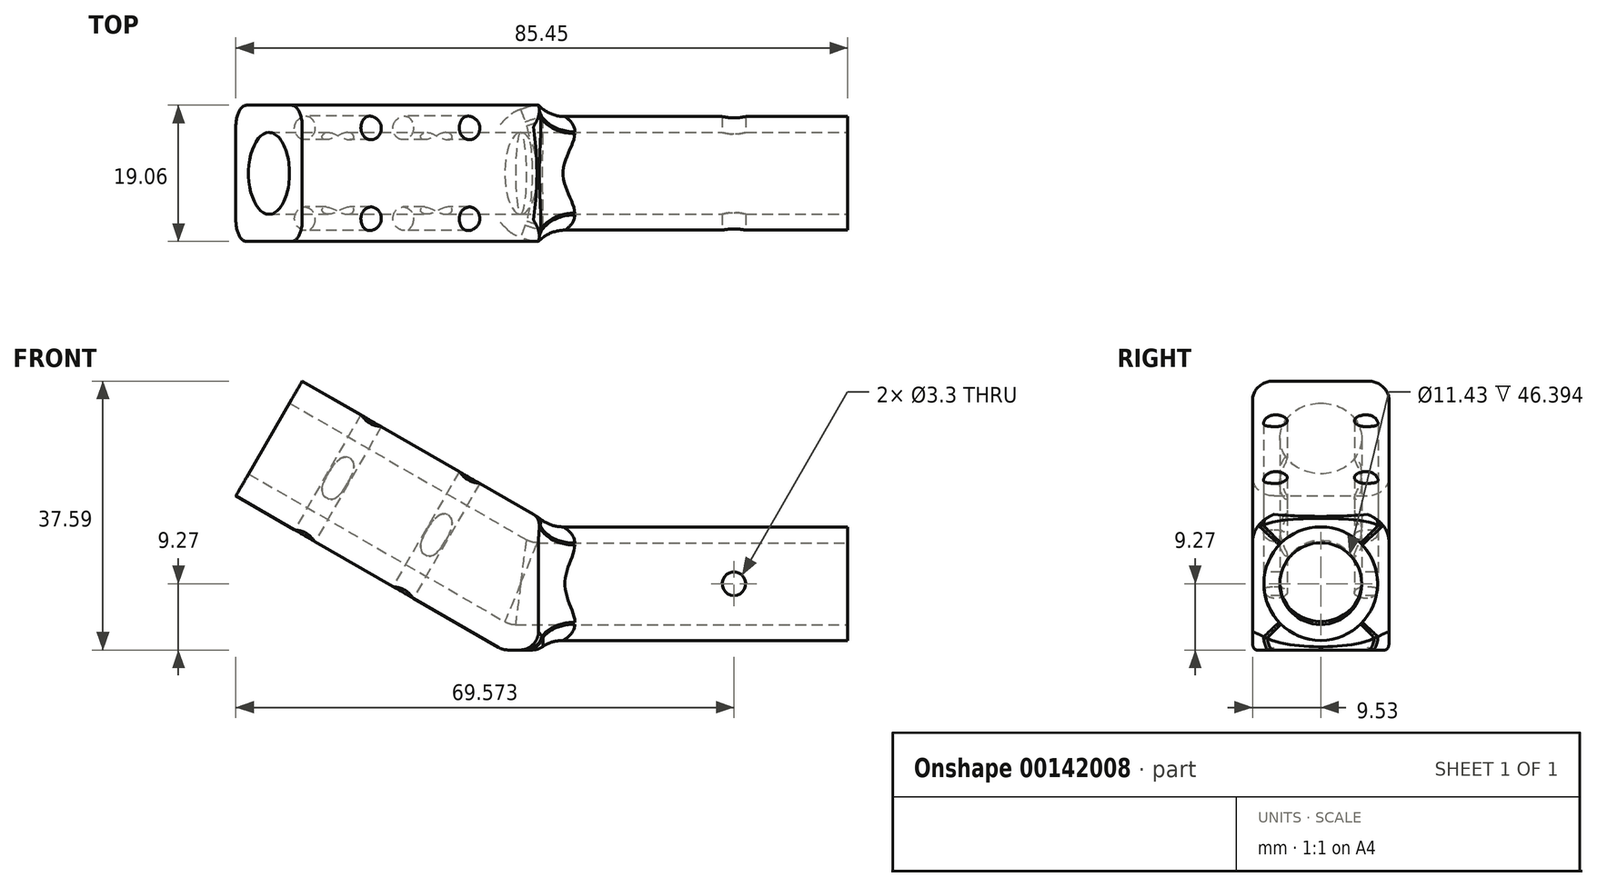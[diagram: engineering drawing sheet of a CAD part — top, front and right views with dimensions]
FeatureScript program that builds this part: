
annotation { "Feature Type Name" : "Feature", "Feature Type Description" : "" }
export const myFeature = defineFeature(function(context is Context, id is Id, definition is map)
    precondition{}
    {
        {
            var Q0;
            Q0=qCreatedBy(makeId("Front.planeOp"),FACE);
            var sketch = newSketch(context, id + "F0", { "sketchPlane" : qUnion([Q0])});
            skLineSegment(sketch, "E0.bottom", {"start": v(4.97, 9.27) * mm, "end": v(48.15, 9.27) * mm});
            skLineSegment(sketch, "E0.top", {"start": v(0, -9.27) * mm, "end": v(48.15, -9.27) * mm});
            skLineSegment(sketch, "E0.right", {"start": v(48.15, 9.27) * mm, "end": v(48.15, -9.27) * mm});
            skLineSegment(sketch, "E1", {"start": v(0, 0) * mm, "end": v(48.15, 0) * mm, "construction": true});
            skLineSegment(sketch, "E2", {"start": v(4.97, 9.27) * mm, "end": v(-28.03, 28.32) * mm});
            skLineSegment(sketch, "E3", {"start": v(-37.3, 12.26) * mm, "end": v(-28.03, 28.32) * mm});
            skPoint(sketch, "E4.orphan", {"position": v(0, 13.5) * mm});
            skLineSegment(sketch, "E5", {"start": v(-37.3, 12.26) * mm, "end": v(0, -9.27) * mm});
            skSolve(sketch);
        }
        {
            var Q0;
            Q0 = qSketchRegion(id + "F0", true);
            extrude(context, id + "F1", {"entities" : qUnion([Q0]), "depth" : 9.52 * mm, "hasSecondDirection" : true, "secondDirectionOppositeDirection" : true, "secondDirectionDepth" : 9.52 * mm});
        }
        {
            var Q0;
            Q0=makeQuery(id+"F1.opExtrude","SWEPT_FACE",FACE,{"disambiguationData":[OSD([sQuery(id+"F0.wireOp",EDGE,"E5")])]});
            var sketch = newSketch(context, id + "F2", { "sketchPlane" : qUnion([Q0])});
            skLineSegment(sketch, "E6.bottom", {"start": v(-38.43, -9.53) * mm, "end": v(-0.33, -9.53) * mm});
            skLineSegment(sketch, "E6.top", {"start": v(-38.43, 9.53) * mm, "end": v(-0.33, 9.53) * mm});
            skLineSegment(sketch, "E6.left", {"start": v(-38.43, -9.53) * mm, "end": v(-38.43, 9.53) * mm});
            skLineSegment(sketch, "E6.right", {"start": v(-0.33, -9.52) * mm, "end": v(-0.33, 9.53) * mm});
            skLineSegment(sketch, "E7", {"start": v(-38.43, 0) * mm, "end": v(-0.33, 0) * mm, "construction": true});
            skLineSegment(sketch, "E8", {"start": v(-19.38, 9.53) * mm, "end": v(-19.38, -9.53) * mm, "construction": true});
            skLineSegment(sketch, "E9.bottom", {"start": v(-27.32, -6.35) * mm, "end": v(-11.45, -6.35) * mm, "construction": true});
            skLineSegment(sketch, "E9.top", {"start": v(-27.32, 6.35) * mm, "end": v(-11.45, 6.35) * mm, "construction": true});
            skLineSegment(sketch, "E9.left", {"start": v(-27.32, -6.35) * mm, "end": v(-27.32, 6.35) * mm, "construction": true});
            skLineSegment(sketch, "E9.right", {"start": v(-11.45, -6.35) * mm, "end": v(-11.45, 6.35) * mm, "construction": true});
            skPoint(sketch, "E9.middle", {"position": v(-19.38, 0) * mm});
            skSolve(sketch);
        }
        {
            var Q0;
            Q0=sQuery(id+"F2.wireOp",VERTEX,"E9.left.end");
            var Q1;
            Q1=sQuery(id+"F2.wireOp",VERTEX,"E9.left.start");
            var Q2;
            Q2=sQuery(id+"F2.wireOp",VERTEX,"E9.right.start");
            var Q3;
            Q3=sQuery(id+"F2.wireOp",VERTEX,"E9.top.end");
            var Q4;
            Q4=makeQuery(id+"F1.opExtrude","SWEPT_BODY",BODY,{"disambiguationData":[OSD([sQuery(id+"F0.wireOp",EDGE,"E0.bottom"),sQuery(id+"F0.wireOp",EDGE,"E0.top"),sQuery(id+"F0.wireOp",EDGE,"E0.right"),sQuery(id+"F0.wireOp",EDGE,"E2"),sQuery(id+"F0.wireOp",EDGE,"95kfVAff-3bN3-xnc1-YnyT-jtpb1TC5GENx"),sQuery(id+"F0.wireOp",EDGE,"E3")])]});
            hole(context, id + "F3", {"style" : HoleStyle.SIMPLE, "endStyle" : HoleEndStyle.THROUGH, "standardTappedOrClearance" : lookupTablePath({ "standard" : "ISO", "fit" : "Normal", "size" : "M3", "type" : "Clearance" }), "standardBlindInLast" : lookupTablePath({ "fit" : "Standard", "standard" : "ISO", "size" : "M3", "type" : "Clearance" }), "holeDiameter" : 3.3 * mm, "locations" : qUnion([Q0, Q1, Q2, Q3]), "scope" : qUnion([Q4]), "isTappedThrough" : true});
        }
        {
            var Q0;
            Q0=makeQuery(id+"F1.opExtrude","SWEPT_FACE",FACE,{"disambiguationData":[OSD([sQuery(id+"F0.wireOp",EDGE,"E3")])]});
            var sketch = newSketch(context, id + "F4", { "sketchPlane" : qUnion([Q0])});
            skLineSegment(sketch, "E10", {"start": v(0, 10.51) * mm, "end": v(0, -8.03) * mm, "construction": true});
            skCircle(sketch, "E11", {"center": v(0, 1.24) * mm, "radius": 5.72 * mm});
            skSolve(sketch);
        }
        {
            var Q0;
            Q0=qCreatedBy(makeId("Front.planeOp"),FACE);
            var sketch = newSketch(context, id + "F5", { "sketchPlane" : qUnion([Q0])});
            skLineSegment(sketch, "E12", {"start": v(-32.66, 20.3) * mm, "end": v(2.48, 0) * mm});
            skLineSegment(sketch, "E13", {"start": v(2.48, 0) * mm, "end": v(48.15, 0) * mm});
            skPoint(sketch, "E14", {"position": v(48.15, 0) * mm});
            skSolve(sketch);
        }
        {
            var Q0;
            Q0 = qSketchRegion(id + "F4", true);
            var Q1;
            Q1 = qConstructionFilter(qBodyType(qCreatedBy(id + "F5" ,EDGE), BodyType.WIRE), ConstructionObject.NO);
            sweep(context, id + "F6", {"operationType" : NewBodyOperationType.REMOVE, "profiles" : qUnion([Q0]), "path" : qUnion([Q1])});
        }
        {
            var Q0;
            Q0=makeQuery(id+"F1.opExtrude","SWEPT_FACE",FACE,{"disambiguationData":[OSD([sQuery(id+"F0.wireOp",EDGE,"E0.right")])]});
            var sketch = newSketch(context, id + "F7", { "sketchPlane" : qUnion([Q0])});
            skCircle(sketch, "E15", {"center": v(0, 0) * mm, "radius": 7.94 * mm});
            skLineSegment(sketch, "E16.0.0", {"start": v(9.53, -9.27) * mm, "end": v(9.53, 9.27) * mm});
            skLineSegment(sketch, "E16.0.1", {"start": v(9.52, 9.27) * mm, "end": v(-9.53, 9.27) * mm});
            skLineSegment(sketch, "E16.0.2", {"start": v(-9.53, 9.27) * mm, "end": v(-9.53, -9.27) * mm});
            skLineSegment(sketch, "E16.0.3", {"start": v(-9.53, -9.27) * mm, "end": v(9.52, -9.27) * mm});
            skSolve(sketch);
        }
        {
            var Q0;
            Q0 = qSketchRegion(id + "F7", true);
            extrude(context, id + "F8", {"entities" : qUnion([Q0]), "operationType" : NewBodyOperationType.REMOVE, "oppositeDirection" : true, "depth" : 43.18 * mm});
        }
        {
            var Q0;
            Q0=makeQuery(id+"F8.boolean.opBoolean","COPY",EDGE,{"derivedFrom":makeQuery(id+"F8.opExtrude","CAP_EDGE",EDGE,{"disambiguationData":[OSD([sQuery(id+"F7.wireOp",EDGE,"E15")])],"isStart":false})});
            fillet(context, id + "F9", {"entities" : qUnion([Q0]), "radius" : 5.08 * mm, "tangentPropagation" : true, "allowEdgeOverflow" : false});
        }
        {
            var Q0;
            Q0=makeQuery(id+"F9.opFillet","BLEND_EDGE",EDGE,{"blendedFrom":[makeQuery(id+"F8.boolean.opBoolean","COPY",EDGE,{"derivedFrom":makeQuery(id+"F8.opExtrude","CAP_EDGE",EDGE,{"disambiguationData":[OSD([sQuery(id+"F7.wireOp",EDGE,"E15")])],"isStart":false})}),makeQuery(id+"F1.opExtrude","SWEPT_FACE",FACE,{"disambiguationData":[OSD([sQuery(id+"F0.wireOp",EDGE,"E2")])]})],"blendedInto":[makeQuery(id+"F1.opExtrude","SWEPT_FACE",FACE,{"disambiguationData":[OSD([sQuery(id+"F0.wireOp",EDGE,"E2")])]})]});
            var Q1;
            Q1=makeQuery(id+"F9.opFillet","BLEND_EDGE",EDGE,{"blendedFrom":[makeQuery(id+"F8.boolean.opBoolean","COPY",EDGE,{"derivedFrom":makeQuery(id+"F8.opExtrude","CAP_EDGE",EDGE,{"disambiguationData":[OSD([sQuery(id+"F7.wireOp",EDGE,"E15")])],"isStart":false})}),makeQuery(id+"F1.opExtrude","SWEPT_FACE",FACE,{"disambiguationData":[OSD([sQuery(id+"F0.wireOp",EDGE,"E0.top")])]})],"blendedInto":[makeQuery(id+"F1.opExtrude","SWEPT_FACE",FACE,{"disambiguationData":[OSD([sQuery(id+"F0.wireOp",EDGE,"E0.top")])]})]});
            fillet(context, id + "F10", {"entities" : qUnion([Q0, Q1]), "radius" : 2.54 * mm, "tangentPropagation" : true, "allowEdgeOverflow" : false});
        }
        {
            var Q0;
            Q0=makeQuery(id+"F1.opExtrude","SWEPT_FACE",FACE,{"disambiguationData":[OSD([sQuery(id+"F0.wireOp",EDGE,"E2")])]});
            var sketch = newSketch(context, id + "F11", { "sketchPlane" : qUnion([Q0])});
            skCircle(sketch, "E17.0", {"center": v(-27.32, -6.35) * mm, "radius": 1.65 * mm});
            skCircle(sketch, "E17.1", {"center": v(-27.32, 6.35) * mm, "radius": 1.65 * mm});
            skCircle(sketch, "E17.2", {"center": v(-11.45, -6.35) * mm, "radius": 1.65 * mm});
            skCircle(sketch, "E17.3", {"center": v(-11.45, 6.35) * mm, "radius": 1.65 * mm});
            skCircle(sketch, "E18", {"center": v(-27.32, -6.35) * mm, "radius": 3.18 * mm});
            skCircle(sketch, "E19", {"center": v(-27.32, 6.35) * mm, "radius": 3.18 * mm});
            skCircle(sketch, "E20", {"center": v(-11.45, 6.35) * mm, "radius": 3.18 * mm});
            skCircle(sketch, "E21", {"center": v(-11.45, -6.35) * mm, "radius": 3.18 * mm});
            skSolve(sketch);
        }
        {
            var Q0;
            Q0=makeQuery(id+"F1.opExtrude","CAP_EDGE",EDGE,{"disambiguationData":[OSD([sQuery(id+"F0.wireOp",EDGE,"E2")])],"isStart":true});
            var Q1;
            Q1=makeQuery(id+"F1.opExtrude","CAP_EDGE",EDGE,{"disambiguationData":[OSD([sQuery(id+"F0.wireOp",EDGE,"E2")])],"isStart":false});
            var Q2;
            Q2=makeQuery(id+"F1.opExtrude","CAP_EDGE",EDGE,{"disambiguationData":[OSD([sQuery(id+"F0.wireOp",EDGE,"E5")])],"isStart":false});
            var Q3;
            Q3=makeQuery(id+"F1.opExtrude","CAP_EDGE",EDGE,{"disambiguationData":[OSD([sQuery(id+"F0.wireOp",EDGE,"E5")])],"isStart":true});
            var Q4;
            Q4=makeQuery(id+"F6.boolean.opBoolean","COPY",EDGE,{"derivedFrom":makeQuery(id+"F6.opSweep","MID_CAP_EDGE",EDGE,{"disambiguationData":[OSD([sQuery(id+"F4.wireOp",EDGE,"E11"),sQuery(id+"F5.wireOp",VERTEX,"E13.start")])],"capPos":1.0})});
            fillet(context, id + "F12", {"entities" : qUnion([Q0, Q1, Q2, Q3, Q4]), "radius" : 3 * mm, "allowEdgeOverflow" : false});
        }
        {
            var Q0;
            Q0=qCreatedBy(makeId("Front.planeOp"),FACE);
            var sketch = newSketch(context, id + "F13", { "sketchPlane" : qUnion([Q0])});
            skCircle(sketch, "E22", {"center": v(32.27, 0) * mm, "radius": 1.65 * mm});
            skSolve(sketch);
        }
        {
            var Q0;
            Q0 = qSketchRegion(id + "F13", true);
            extrude(context, id + "F14", {"entities" : qUnion([Q0]), "operationType" : NewBodyOperationType.REMOVE, "endBound" : BoundingType.THROUGH_ALL, "oppositeDirection" : true, "depth" : 25.4 * mm, "hasSecondDirection" : true, "secondDirectionOppositeDirection" : false, "secondDirectionDepth" : 25.4 * mm});
        }
        {
            var Q0;
            Q0=makeQuery(id+"F1.opExtrude","SWEPT_EDGE",EDGE,{"disambiguationData":[OSD([sQuery(id+"F0.wireOp",EDGE,"E0.top"),sQuery(id+"F0.wireOp",EDGE,"E5")])]});
            var Q1;
            Q1=makeQuery(id+"F9.opFillet","BLEND_EDGE",EDGE,{"blendedFrom":[makeQuery(id+"F8.boolean.opBoolean","COPY",EDGE,{"derivedFrom":makeQuery(id+"F8.opExtrude","CAP_EDGE",EDGE,{"disambiguationData":[OSD([sQuery(id+"F7.wireOp",EDGE,"E15")])],"isStart":false})}),makeQuery(id+"F1.opExtrude","SWEPT_FACE",FACE,{"disambiguationData":[OSD([sQuery(id+"F0.wireOp",EDGE,"E0.top")])]})],"blendedInto":[makeQuery(id+"F1.opExtrude","SWEPT_FACE",FACE,{"disambiguationData":[OSD([sQuery(id+"F0.wireOp",EDGE,"E0.top")])]})]});
            fillet(context, id + "F15", {"entities" : qUnion([Q0, Q1]), "radius" : 2.54 * mm, "allowEdgeOverflow" : false});
        }
    });
